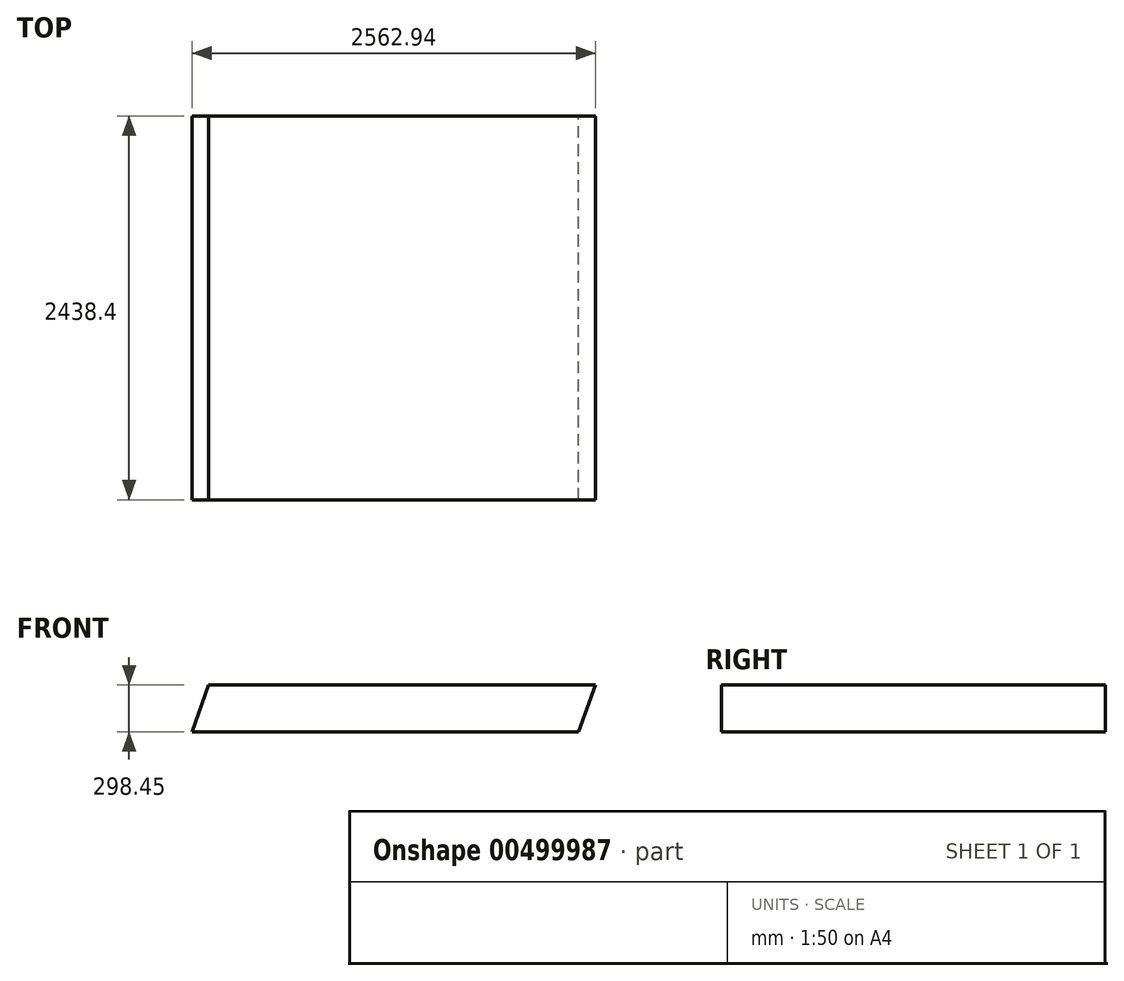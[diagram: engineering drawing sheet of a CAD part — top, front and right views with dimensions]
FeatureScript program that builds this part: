
annotation { "Feature Type Name" : "Feature", "Feature Type Description" : "" }
export const myFeature = defineFeature(function(context is Context, id is Id, definition is map)
    precondition{}
    {
        {
            var Q0;
            Q0=qCreatedBy(makeId("Front.planeOp"),FACE);
            var sketch = newSketch(context, id + "F0", { "sketchPlane" : qUnion([Q0])});
            skLineSegment(sketch, "E0.bottom", {"start": v(-1803.4, 149.23) * mm, "end": v(1803.4, 149.23) * mm});
            skLineSegment(sketch, "E0.top", {"start": v(-1803.4, -149.23) * mm, "end": v(1803.4, -149.23) * mm});
            skLineSegment(sketch, "E0.left", {"start": v(-1803.4, 149.23) * mm, "end": v(-1803.4, -149.23) * mm});
            skLineSegment(sketch, "E0.right", {"start": v(1803.4, 149.23) * mm, "end": v(1803.4, -149.23) * mm});
            skPoint(sketch, "E0.middle", {"position": v(0, 0) * mm});
            skLineSegment(sketch, "E1", {"start": v(-1803.4, -149.23) * mm, "end": v(-1701.8, 149.23) * mm});
            skLineSegment(sketch, "E2", {"start": v(1917.22, -149.23) * mm, "end": v(1561.62, 149.23) * mm});
            skLineSegment(sketch, "E3", {"start": v(1600.2, -149.23) * mm, "end": v(1244.6, 149.23) * mm});
            skLineSegment(sketch, "E4", {"start": v(1244.6, 149.23) * mm, "end": v(1244.6, -149.23) * mm});
            skLineSegment(sketch, "E5", {"start": v(1561.62, 149.23) * mm, "end": v(1603.9, -149.23) * mm});
            skLineSegment(sketch, "E6", {"start": v(1285.32, -149.23) * mm, "end": v(1394.17, 149.23) * mm});
            skLineSegment(sketch, "E7", {"start": v(-1168.77, -149.23) * mm, "end": v(-1063.08, 149.23) * mm});
            skSolve(sketch);
        }
        {
            var Q0;
            {var subQ0=sQuery(id+"F0.wireOp",EDGE,"ttIF5d46-imGF-XYFO-nJvS-iFCkjU0lxnrs");Q0=makeQuery(id+"F0.imprint","IMPRINT",FACE,{"disambiguationData":[TD([[makeQuery(id+"F0.imprint","IMPRINT",EDGE,{"derivedFrom":subQ0}),1.0]])]});}
            var Q1;
            {var subQ0=sQuery(id+"F0.wireOp",EDGE,"E4");Q1=makeQuery(id+"F0.imprint","IMPRINT",FACE,{"disambiguationData":[TD([[makeQuery(id+"F0.imprint","IMPRINT",EDGE,{"derivedFrom":subQ0}),1.0]])]});}
            var Q2;
            {var subQ0=sQuery(id+"F0.wireOp",EDGE,"yBC2yoDI-Mb1E-7Szt-HHTF-cZDUXv2HW0Jr");var subQ3=sQuery(id+"F0.wireOp",EDGE,"E3");var subQ5=makeQuery(id+"F0.imprint","INTERSECT",VERTEX,{"derivedFrom":[subQ3,subQ0]});Q2=makeQuery(id+"F0.imprint","IMPRINT",FACE,{"disambiguationData":[TD([[makeQuery(id+"F0.imprint","IMPRINT",EDGE,{"disambiguationData":[TD([[subQ5,-1.0]])],"derivedFrom":subQ3}),-1.0]])]});}
            var Q3;
            {var subQ0=sQuery(id+"F0.wireOp",EDGE,"E3");var subQ3=sQuery(id+"F0.wireOp",EDGE,"iKK6oOQe-tG84-mFLb-b1zI-E8EnM6x0omlW");var subQ5=makeQuery(id+"F0.imprint","INTERSECT",VERTEX,{"derivedFrom":[subQ0,subQ3]});Q3=makeQuery(id+"F0.imprint","IMPRINT",FACE,{"disambiguationData":[TD([[makeQuery(id+"F0.imprint","IMPRINT",EDGE,{"disambiguationData":[TD([[subQ5,-1.0]])],"derivedFrom":subQ3}),1.0]])]});}
            var Q4;
            {var subQ2=sQuery(id+"F0.wireOp",EDGE,"E4");Q4=makeQuery(id+"F0.imprint","IMPRINT",FACE,{"disambiguationData":[TD([[makeQuery(id+"F0.imprint","IMPRINT",EDGE,{"derivedFrom":subQ2}),-1.0]])]});}
            extrude(context, id + "F1", {"entities" : qUnion([Q0, Q1, Q2, Q3, Q4]), "depth" : 2438.4 * mm, "offsetDistance" : 25.4 * mm});
        }
    });
